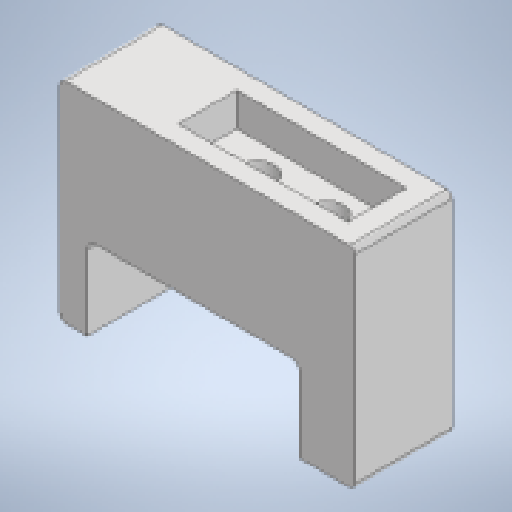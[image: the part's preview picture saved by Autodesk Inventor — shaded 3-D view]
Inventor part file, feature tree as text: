
AUTODESK INVENTOR PART (.ipt)
format: ipt  version: 2023 (Build 270158000, 158)  size: 195,584 bytes
history: native  units: in
note: dims shown in document units (in); Inventor stores cm internally (conversion verified against a paired STEP export)
features: extrude x6, sketch x5, fillet x2
ambient origin geometry x8: Origin, YZ Plane, XZ Plane, XY Plane, X Axis, Y Axis, Z Axis, Center Point
bodies: Solid1 (feature_tree)
feature tree (13):
  sketch  "Sketch1"  dims[d0=0.7874in d1=2.3622in]
  extrude  "Extrusion1"  Depth=0.7874in
  extrude  "Extrusion2"  Depth=0.0197in
  extrude  "Extrusion3"  Depth=0.0197in
  extrude  "Extrusion4"  Depth=1.811in
  extrude  "Extrusion5"  Depth=1.378in
  extrude  "Extrusion6"  Depth=0.3937in TaperAngle=0.0deg
  fillet  "Fillet1"  Radius=1.3937in
  fillet  "Fillet2"  Radius=0.3937in
  sketch  "Sketch2"  dims[d2=0.0197in d3=0.0197in]
  sketch  "Sketch3"  dims[d4=0.0197in d5=0.0197in]
  sketch  "Sketch4"  dims[d6=0.1417in d7=1.811in]
  sketch  "Sketch5"  dims[d9=4.1811in d10=1.378in d11=0.3937in d12=0.0in d13=1.3937in d14=0.0in d15=0.3937in d16=0.0787in d17=0.0in d18=0.0in d19=0.3937in d20=1.1969in d21=0.0in d22=0.0in d23=3.0in d24=0.125in d25=0.7874in d26=1.1811in d27=0.3937in d28=0.0in d29=0.2362in d30=0.9843in d31=0.3937in d32=0.0in d34=0.4724in d35=0.3937in d36=0.0in d37=0.0787in d38=0.0787in d43=0.3937in]
